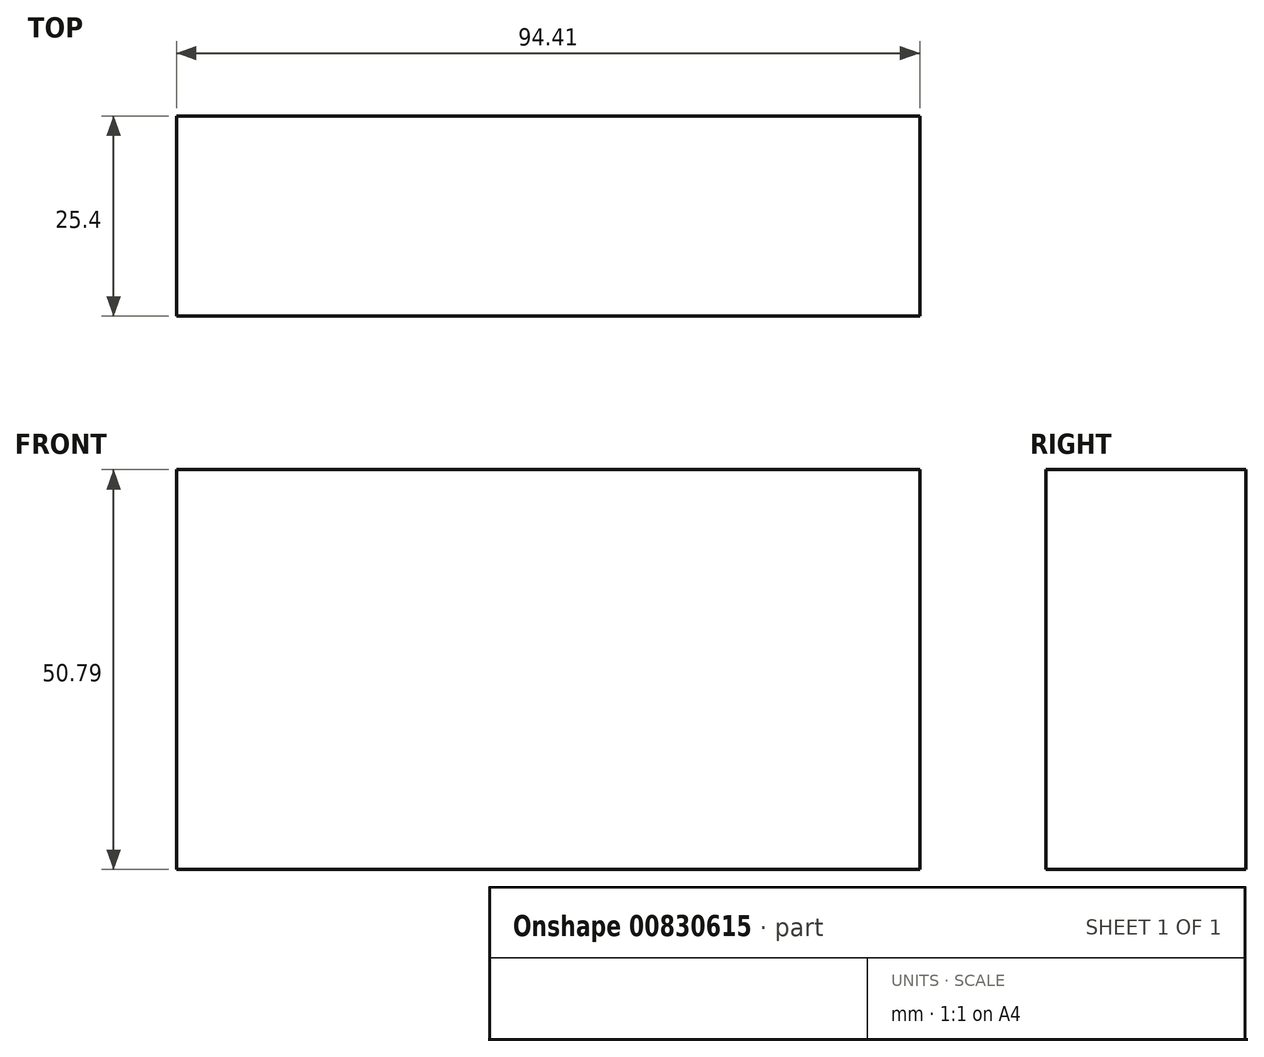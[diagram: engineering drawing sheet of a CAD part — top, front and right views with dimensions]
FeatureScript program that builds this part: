
annotation { "Feature Type Name" : "Feature", "Feature Type Description" : "" }
export const myFeature = defineFeature(function(context is Context, id is Id, definition is map)
    precondition{}
    {
        {
            var Q0;
            Q0=qCreatedBy(makeId("Front.planeOp"),FACE);
            var sketch = newSketch(context, id + "F0", { "sketchPlane" : qUnion([Q0])});
            skLineSegment(sketch, "E0.bottom", {"start": v(0, 0) * mm, "end": v(94.4, 0) * mm});
            skLineSegment(sketch, "E0.top", {"start": v(0, 50.8) * mm, "end": v(94.4, 50.8) * mm});
            skLineSegment(sketch, "E0.left", {"start": v(0, 0) * mm, "end": v(0, 50.8) * mm});
            skLineSegment(sketch, "E0.right", {"start": v(94.4, 0) * mm, "end": v(94.4, 50.8) * mm});
            skSolve(sketch);
        }
        {
            var Q0;
            Q0=makeQuery(id+"F0.imprint","IMPRINT",FACE,{"disambiguationData":[TD([[makeQuery(id+"F0.imprint","IMPRINT",EDGE,{"derivedFrom":sQuery(id+"F0.wireOp",EDGE,"E0.bottom")}),1.0]])]});
            extrude(context, id + "F1", {"entities" : qUnion([Q0]), "depth" : 25.4 * mm, "offsetDistance" : 25.4 * mm});
        }
    });
